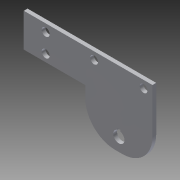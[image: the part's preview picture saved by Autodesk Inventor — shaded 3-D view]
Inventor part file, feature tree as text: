
AUTODESK INVENTOR PART (.ipt)
format: ipt  version: 2013 (Build 170138000, 138)  size: 161,280 bytes
history: native  units: in
note: dims shown in document units (in); Inventor stores cm internally (conversion verified against a paired STEP export)
features: sketch x5, other x5, reference x4, sheet_metal_op x1, extrude x1, fillet x1
ambient origin geometry x8: Origin, YZ Plane, XZ Plane, XY Plane, X Axis, Y Axis, Z Axis, Center Point
feature tree (17):
  sheet_metal_op  "Face3"
  extrude  "Extrusion2"  Depth=0.25in
  sketch  "Sketch8"  dims[d8=0.125in]
  fillet  "Fillet1"  Radius=0.295in
  sketch  "Sketch11"  dims[d60=2.5in d61=0.4375in d62=0.375in d63=0.125in d67=0.125in d68=0.0in d69=2.053in d70=0.0in d71=1.125in d72=2.053in d75=0.125in d76=0.0in d77=0.125in d78=0.0in d79=0.125in d80=0.0in d81=1.0in d82=0.0469in d86=0.0938in d87=0.0469in]
  other  "Plate6"
  sketch  "Sketch7"  dims[d3=0.295in d4=0.25in d5=0.295in]
  reference  "Reference1"
  reference  "Reference2"
  sketch  "Sketch9"  dims[d19=0.25in]
  sketch  "Sketch10"  dims[d56=0.125in]
  reference  "Reference3"
  reference  "Reference4"
  other  "Cut1"
  other  "Cut3"
  other  "Cut4"
  other  "Cut5"
